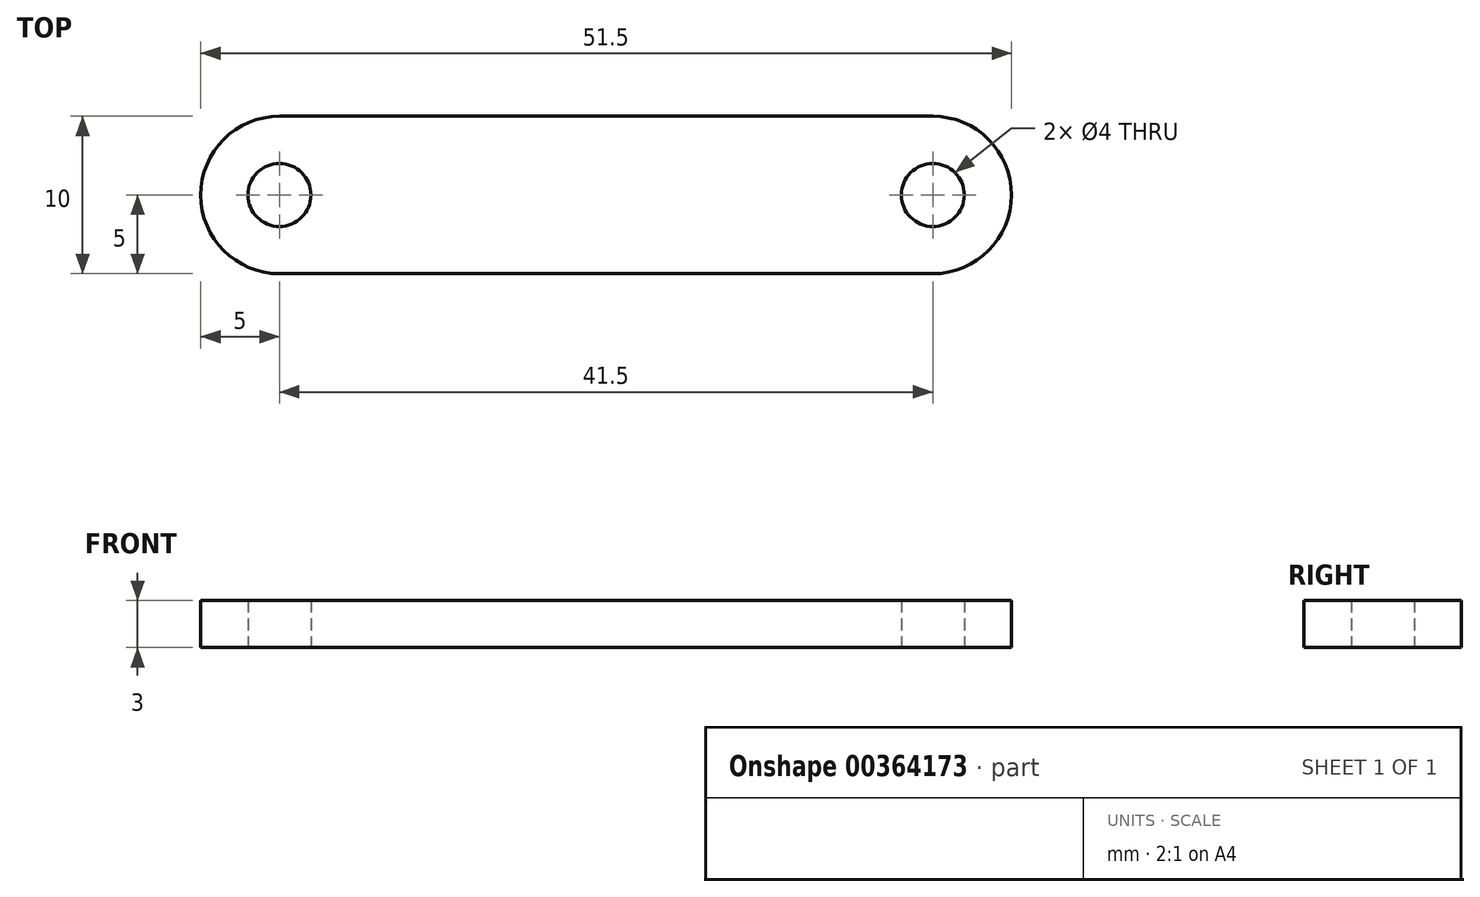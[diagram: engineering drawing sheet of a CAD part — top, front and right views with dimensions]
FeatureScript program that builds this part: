
annotation { "Feature Type Name" : "Feature", "Feature Type Description" : "" }
export const myFeature = defineFeature(function(context is Context, id is Id, definition is map)
    precondition{}
    {
        {
            var Q0;
            Q0=qCreatedBy(makeId("Top.planeOp"),FACE);
            var sketch = newSketch(context, id + "F0", { "sketchPlane" : qUnion([Q0])});
            skLineSegment(sketch, "E0.bottom", {"start": v(20.75, 5) * mm, "end": v(-20.75, 5) * mm});
            skLineSegment(sketch, "E0.top", {"start": v(20.75, -5) * mm, "end": v(-20.75, -5) * mm});
            skPoint(sketch, "E0.middle", {"position": v(0, 0) * mm});
            skCircle(sketch, "E1", {"center": v(-20.75, 0) * mm, "radius": 2 * mm});
            skCircle(sketch, "E2", {"center": v(20.75, 0) * mm, "radius": 2 * mm});
            skArc(sketch, "E3", {"start": v(-20.75, 5) * mm, "mid": v(-25.75, 0) * mm, "end": v(-20.75, -5) * mm});
            skArc(sketch, "E4", {"start": v(20.75, -5) * mm, "mid": v(25.75, 0) * mm, "end": v(20.75, 5) * mm});
            skSolve(sketch);
        }
        {
            var Q0;
            Q0=qSketchRegion(id+"F0",true);
            extrude(context, id + "F1", {"entities" : qUnion([Q0]), "depth" : 3 * mm});
        }
    });
